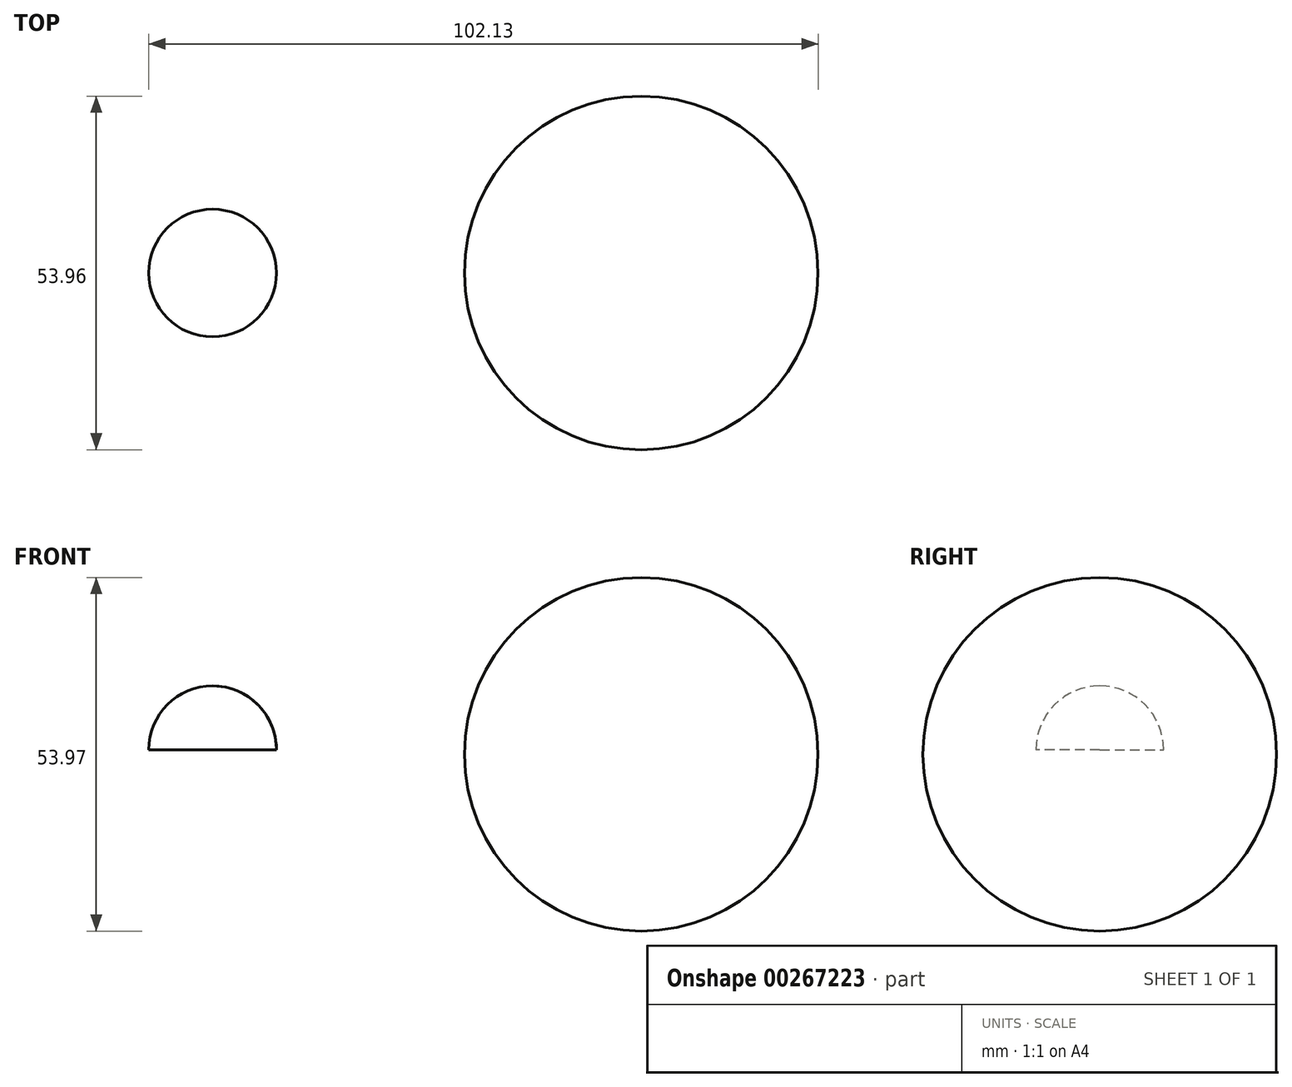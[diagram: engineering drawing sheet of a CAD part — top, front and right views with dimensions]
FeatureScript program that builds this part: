
annotation { "Feature Type Name" : "Feature", "Feature Type Description" : "" }
export const myFeature = defineFeature(function(context is Context, id is Id, definition is map)
    precondition{}
    {
        {
            var Q0;
            Q0=qCreatedBy(makeId("Front.planeOp"),FACE);
            var sketch = newSketch(context, id + "F0", { "sketchPlane" : qUnion([Q0])});
            skCircle(sketch, "E0", {"center": v(-10.36, 19.96) * mm, "radius": 26.98 * mm});
            skLineSegment(sketch, "E1", {"start": v(-10.36, 46.95) * mm, "end": v(-10.36, -7.02) * mm});
            skSolve(sketch);
        }
        {
            var Q0;
            {var subQ0=sQuery(id+"F0.wireOp",EDGE,"E1");Q0=makeQuery(id+"F0.imprint","IMPRINT",FACE,{"disambiguationData":[TD([[makeQuery(id+"F0.imprint","IMPRINT",EDGE,{"derivedFrom":subQ0}),1.0]])]});}
            var Q1;
            Q1=sQuery(id+"F0.wireOp",EDGE,"E1");
            revolve(context, id + "F1", {"entities" : qUnion([Q0]), "axis" : qUnion([Q1]), "revolveType" : RevolveType.FULL});
        }
        {
            var Q0;
            Q0=qCreatedBy(makeId("Front.planeOp"),FACE);
            var sketch = newSketch(context, id + "F2", { "sketchPlane" : qUnion([Q0])});
            skCircle(sketch, "E2", {"center": v(-75.76, 20.67) * mm, "radius": 9.74 * mm});
            skLineSegment(sketch, "E3", {"start": v(-75.76, 20.67) * mm, "end": v(-75.76, 30.4) * mm});
            skLineSegment(sketch, "E4", {"start": v(-75.76, 20.67) * mm, "end": v(-66.03, 20.67) * mm});
            skSolve(sketch);
        }
        {
            var Q0;
            {var subQ0=sQuery(id+"F2.wireOp",EDGE,"E3");Q0=makeQuery(id+"F2.imprint","IMPRINT",FACE,{"disambiguationData":[TD([[makeQuery(id+"F2.imprint","IMPRINT",EDGE,{"derivedFrom":subQ0}),-1.0]])]});}
            var Q1;
            Q1=sQuery(id+"F2.wireOp",EDGE,"E3");
            revolve(context, id + "F3", {"entities" : qUnion([Q0]), "axis" : qUnion([Q1]), "revolveType" : RevolveType.FULL});
        }
    });
